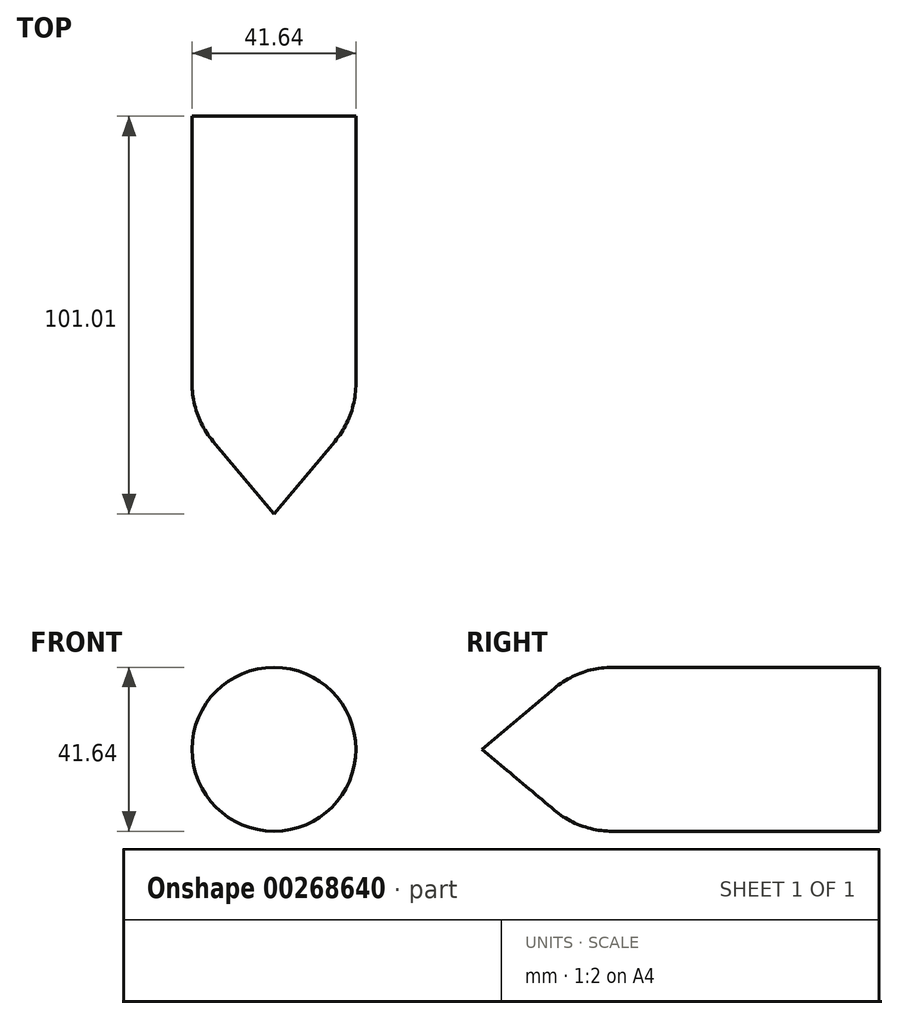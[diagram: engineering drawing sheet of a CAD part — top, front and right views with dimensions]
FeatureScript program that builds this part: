
annotation { "Feature Type Name" : "Feature", "Feature Type Description" : "" }
export const myFeature = defineFeature(function(context is Context, id is Id, definition is map)
    precondition{}
    {
        {
            var Q0;
            Q0=qCreatedBy(makeId("Front.planeOp"),FACE);
            var sketch = newSketch(context, id + "F0", { "sketchPlane" : qUnion([Q0])});
            skCircle(sketch, "E0", {"center": v(0, 0) * mm, "radius": 20.82 * mm});
            skSolve(sketch);
        }
        {
            var Q0;
            Q0 = qSketchRegion(id + "F0", true);
            extrude(context, id + "F1", {"entities" : qUnion([Q0]), "depth" : 76.2 * mm});
        }
        {
            var Q0;
            Q0=makeQuery(id+"F1.opExtrude","CAP_FACE",FACE,{"disambiguationData":[OSD([sQuery(id+"F0.wireOp",EDGE,"E0")])],"isStart":false});
            extrude(context, id + "F2", {"entities" : qUnion([Q0]), "operationType" : NewBodyOperationType.ADD, "depth" : 25.4 * mm, "hasDraft" : true, "draftAngle" : 40 * degree, "draftPullDirection" : true});
        }
        {
            var Q0;
            Q0=makeQuery(id+"F2.opExtrude","SWEPT_FACE",FACE,{"disambiguationData":[OSD([sQuery(id+"F0.wireOp",EDGE,"E0")])]});
            var Q1;
            {var subQ0=sQuery(id+"F0.wireOp",EDGE,"E0");Q1=makeQuery(id+"F2.boolean.opBoolean","MERGE",EDGE,{"derivedFrom":[makeQuery(id+"F1.opExtrude","CAP_EDGE",EDGE,{"disambiguationData":[OSD([subQ0])],"isStart":false}),makeQuery(id+"F2.opExtrude","CAP_EDGE",EDGE,{"disambiguationData":[OSD([subQ0])],"isStart":true})]});}
            fillet(context, id + "F3", {"entities" : qUnion([Q0, Q1]), "radius" : 22.86 * mm, "tangentPropagation" : true, "allowEdgeOverflow" : false});
        }
    });
